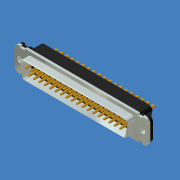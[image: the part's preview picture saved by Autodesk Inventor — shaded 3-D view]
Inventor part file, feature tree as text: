
AUTODESK INVENTOR PART (.ipt)
format: ipt  version: 2019 (Build 230136000, 136)  size: 701,952 bytes
history: native  units: mm (DEFAULTED — no unit token found)
features: extrude x14, pattern_linear x7, sketch x4, fillet x4, chamfer x3
ambient origin geometry x8: Origin, YZ Plane, XZ Plane, XY Plane, X Axis, Y Axis, Z Axis, Center Point
bodies: Solid1 (feature_tree)
feature tree (32):
  sketch  "Sketch1"  dims[d0=1.745329mm d6=0.381mm d7=2.418418mm d8=0.855895mm d9=2.418418mm]
  extrude  "Extrusion1"  Depth=0.381mm
  extrude  "Extrusion2"  Depth=1.397mm
  fillet  "Fillet4"  Radius=1.397mm
  extrude  "Pin1"  Depth=5.08mm TaperAngle=0.0deg
  extrude  "Pin2"  Depth=5.08mm TaperAngle=0.0deg
  extrude  "Pin50"  Depth=10.8966mm
  fillet  "Fillet1"  Radius=2.794mm
  fillet  "Fillet2"  Radius=180.0mm
  fillet  "Fillet50"  Radius=2.794mm
  extrude  "Extrusion5"  Depth=1.909443mm
  extrude  "Extrusion6"  Depth=0.254mm
  sketch  "Sketch4"  dims[d24=5.08mm d25=0.0mm d26=5.08mm d27=0.0mm d28=190.0mm d30=2.794mm d31=180.0mm d33=2.794mm d34=1.909443mm d35=0.254mm d36=1.6002mm d37=0.0mm d38=5.08mm d39=0.0mm d40=5.08mm d41=0.0mm d42=5.08mm d43=0.0mm d44=0.4953mm d45=0.4953mm d46=1.016mm d47=0.3048mm d48=0.3048mm d49=0.3048mm d50=0.3048mm d52=2.8448mm d53=5.08mm d54=0.0mm d55=0.4953mm d56=5.08mm d57=0.0mm d58=0.2032mm d59=0.2032mm d60=190.0mm d62=2.794mm d63=0.381mm d64=20.0mm d66=2.794mm d67=5.1054mm d68=0.0mm d69=5.6388mm d70=0.0mm d71=5.6388mm d72=0.0mm d73=5.6388mm d74=0.0mm d75=190.0mm d77=2.794mm d78=180.0mm d80=2.794mm d81=190.0mm d83=2.794mm d86=1.909443mm d87=10.8966mm d88=57.9628mm d89=45.0deg d90=45.0deg d91=45.0deg]
  extrude  "Extrusion7"  Depth=1.6002mm TaperAngle=0.0deg
  extrude  "Extrusion8"  Depth=5.08mm TaperAngle=0.0deg
  extrude  "ExtrudeSgr50"  Depth=5.08mm TaperAngle=0.0deg
  chamfer  "Chamfer1"  Distance=5.08mm
  chamfer  "Chamfer2"  Distance=0.4953mm
  chamfer  "Chamfer50"  Distance=0.4953mm
  pattern_linear  "Pattern1"  Spacing1=1.016mm  [1 undecoded]
  pattern_linear  "Pattern2"  Spacing1=0.3048mm  [1 undecoded]
  pattern_linear  "Pattern50"  Spacing1=0.3048mm  [1 undecoded]
  pattern_linear  "Pattern15"  Spacing1=0.3048mm  [1 undecoded]
  extrude  "Female"  Depth=10.8966mm
  extrude  "Socket1"  Depth=2.8448mm
  extrude  "Socket2"  Depth=5.08mm
  extrude  "Socket50"  TaperAngle=0.0deg  [1 undecoded]
  pattern_linear  "Pattern5"  Spacing1=0.4953mm  [1 undecoded]
  pattern_linear  "Pattern6"  Spacing1=5.08mm  [1 undecoded]
  pattern_linear  "Pattern7"  Spacing1=0.0mm  [1 undecoded]
  sketch  "Sketch2"  dims[d11=1.314425mm d15=2.54mm d19=1.397mm]
  sketch  "Sketch3"  dims[d20=1.27mm d21=0.0mm d22=5.08mm d23=0.0mm]
note: 8 required parameter values undecoded (feature->parameter linkage not recoverable at this tier; creation-order binding heuristic only, values carry confidence <= 0.55)
